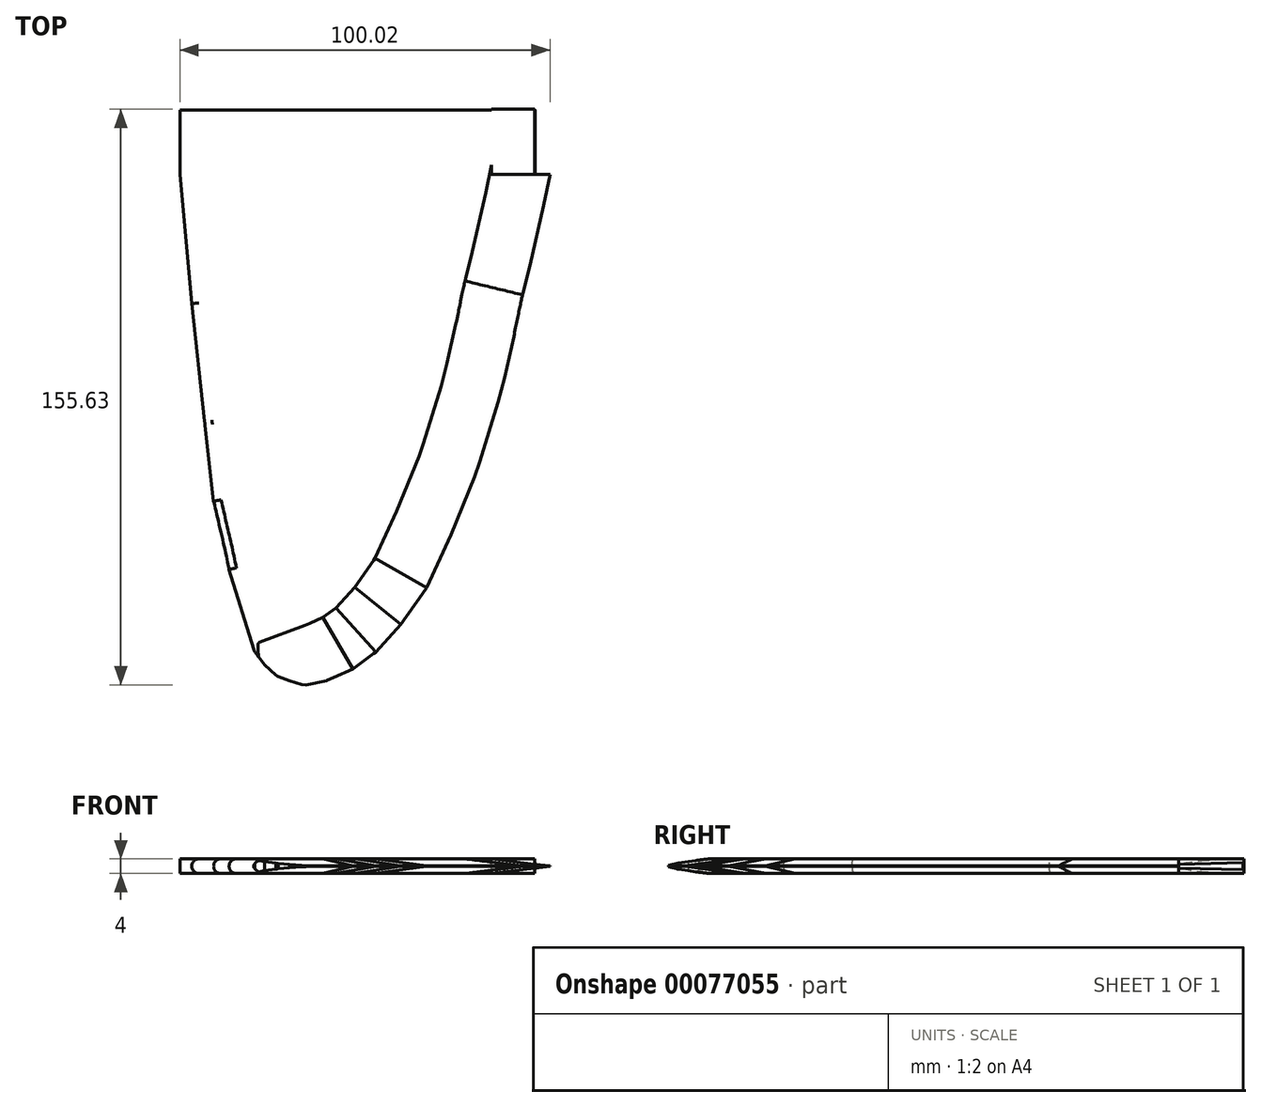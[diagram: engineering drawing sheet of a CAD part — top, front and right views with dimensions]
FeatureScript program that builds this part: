
annotation { "Feature Type Name" : "Feature", "Feature Type Description" : "" }
export const myFeature = defineFeature(function(context is Context, id is Id, definition is map)
    precondition{}
    {
        {
            var Q0;
            Q0=qCreatedBy(makeId("Top.planeOp"),FACE);
            var sketch = newSketch(context, id + "F0", { "sketchPlane" : qUnion([Q0])});
            skLineSegment(sketch, "E0", {"start": v(-143.06, 60.22) * mm, "end": v(-139.92, 25.33) * mm});
            skLineSegment(sketch, "E1", {"start": v(-139.92, 25.33) * mm, "end": v(-136.43, -6.42) * mm});
            skLineSegment(sketch, "E2", {"start": v(-136.43, -6.42) * mm, "end": v(-133.98, -28.05) * mm});
            skLineSegment(sketch, "E3", {"start": v(-133.98, -28.05) * mm, "end": v(-129.8, -46.54) * mm});
            skLineSegment(sketch, "E4", {"start": v(-129.8, -46.54) * mm, "end": v(-123.17, -68.17) * mm});
            skLineSegment(sketch, "E5", {"start": v(-116.54, -75.5) * mm, "end": v(-109.91, -77.94) * mm});
            skLineSegment(sketch, "E6", {"start": v(-109.91, -77.94) * mm, "end": v(-103.28, -76.55) * mm});
            skLineSegment(sketch, "E7", {"start": v(-103.28, -76.55) * mm, "end": v(-96.3, -73.4) * mm});
            skLineSegment(sketch, "E8", {"start": v(-96.3, -73.4) * mm, "end": v(-89.68, -68.52) * mm});
            skLineSegment(sketch, "E9", {"start": v(-89.68, -68.52) * mm, "end": v(-83.05, -61.2) * mm});
            skLineSegment(sketch, "E10", {"start": v(-83.05, -61.2) * mm, "end": v(-76.42, -51.43) * mm});
            skLineSegment(sketch, "E11", {"start": v(-76.42, -51.43) * mm, "end": v(-69.79, -37.12) * mm});
            skLineSegment(sketch, "E12", {"start": v(-69.79, -37.12) * mm, "end": v(-62.81, -20.03) * mm});
            skLineSegment(sketch, "E13", {"start": v(-62.81, -20.03) * mm, "end": v(-56.18, 1.6) * mm});
            skLineSegment(sketch, "E14", {"start": v(-56.18, 1.6) * mm, "end": v(-49.55, 30.91) * mm});
            skLineSegment(sketch, "E15", {"start": v(-49.55, 30.91) * mm, "end": v(-42.92, 60.22) * mm});
            skLineSegment(sketch, "E16", {"start": v(-42.92, 60.22) * mm, "end": v(-47.11, 60.22) * mm});
            skLineSegment(sketch, "E17", {"start": v(-47.11, 60.22) * mm, "end": v(-47.11, 77.66) * mm});
            skLineSegment(sketch, "E18", {"start": v(-47.11, 77.66) * mm, "end": v(-143.06, 77.66) * mm});
            skLineSegment(sketch, "E19", {"start": v(-143.06, 77.66) * mm, "end": v(-143.06, 60.22) * mm});
            skLineSegment(sketch, "E20", {"start": v(-143.08, 77.94) * mm, "end": v(-143.08, 57.6) * mm});
            skLineSegment(sketch, "E21", {"start": v(-143.08, 57.6) * mm, "end": v(-139.68, 22.63) * mm});
            skLineSegment(sketch, "E22", {"start": v(-139.68, 22.63) * mm, "end": v(-136.03, -10.25) * mm});
            skLineSegment(sketch, "E23", {"start": v(-136.03, -10.25) * mm, "end": v(-134.73, -24.08) * mm});
            skLineSegment(sketch, "E24", {"start": v(-134.73, -24.08) * mm, "end": v(-134.07, -28.51) * mm});
            skLineSegment(sketch, "E25", {"start": v(-134.07, -28.51) * mm, "end": v(-129.64, -47.95) * mm});
            skLineSegment(sketch, "E26", {"start": v(-129.64, -47.95) * mm, "end": v(-123.12, -68.44) * mm});
            skLineSegment(sketch, "E27", {"start": v(-123.12, -68.44) * mm, "end": v(-120.25, -72.35) * mm});
            skLineSegment(sketch, "E28", {"start": v(-120.25, -72.35) * mm, "end": v(-116.6, -75.61) * mm});
            skLineSegment(sketch, "E29", {"start": v(-116.6, -75.61) * mm, "end": v(-110.2, -77.7) * mm});
            skLineSegment(sketch, "E30", {"start": v(-110.2, -77.7) * mm, "end": v(-106.8, -77.83) * mm});
            skLineSegment(sketch, "E31", {"start": v(-106.8, -77.83) * mm, "end": v(-103.28, -76.52) * mm});
            skLineSegment(sketch, "E32", {"start": v(-103.28, -76.52) * mm, "end": v(-96.1, -73.4) * mm});
            skLineSegment(sketch, "E33", {"start": v(-96.1, -73.4) * mm, "end": v(-90.1, -68.83) * mm});
            skLineSegment(sketch, "E34", {"start": v(-90.1, -68.83) * mm, "end": v(-83.32, -61.4) * mm});
            skLineSegment(sketch, "E35", {"start": v(-83.32, -61.4) * mm, "end": v(-76.15, -51.08) * mm});
            skLineSegment(sketch, "E36", {"start": v(-76.15, -51.08) * mm, "end": v(-71.32, -40.78) * mm});
            skLineSegment(sketch, "E37", {"start": v(-71.32, -40.78) * mm, "end": v(-66.89, -30.6) * mm});
            skLineSegment(sketch, "E38", {"start": v(-66.89, -30.6) * mm, "end": v(-63.5, -21.73) * mm});
            skLineSegment(sketch, "E39", {"start": v(-63.5, -21.73) * mm, "end": v(-60.62, -13.38) * mm});
            skLineSegment(sketch, "E40", {"start": v(-60.62, -13.38) * mm, "end": v(-57.23, -1.9) * mm});
            skLineSegment(sketch, "E41", {"start": v(-57.23, -1.9) * mm, "end": v(-54.36, 9.06) * mm});
            skLineSegment(sketch, "E42", {"start": v(-54.36, 9.06) * mm, "end": v(-50.45, 27.71) * mm});
            skLineSegment(sketch, "E43", {"start": v(-50.45, 27.71) * mm, "end": v(-46.92, 41.94) * mm});
            skLineSegment(sketch, "E44", {"start": v(-46.92, 41.94) * mm, "end": v(-43.01, 60.33) * mm});
            skLineSegment(sketch, "E45", {"start": v(-43.01, 60.33) * mm, "end": v(-47.06, 60.46) * mm});
            skLineSegment(sketch, "E46", {"start": v(-47.06, 60.46) * mm, "end": v(-47.06, 77.94) * mm});
            skLineSegment(sketch, "E47", {"start": v(-47.06, 77.94) * mm, "end": v(-143.08, 77.94) * mm});
            skFitSpline(sketch, "E48", {"points": [v(-143.06, 60.22) * mm, v(-143.08, 57.6) * mm, v(-139.92, 25.33) * mm, v(-139.68, 22.63) * mm, v(-136.43, -6.42) * mm, v(-136.03, -10.25) * mm, v(-134.73, -24.08) * mm, v(-133.98, -28.05) * mm, v(-129.8, -46.54) * mm, v(-129.64, -47.95) * mm, v(-123.17, -68.17) * mm, v(-120.25, -72.35) * mm, v(-116.54, -75.5) * mm, v(-109.91, -77.94) * mm, v(-106.8, -77.83) * mm, v(-103.28, -76.55) * mm, v(-96.1, -73.4) * mm, v(-90.1, -68.83) * mm, v(-83.32, -61.4) * mm, v(-76.15, -51.08) * mm, v(-71.32, -40.78) * mm, v(-69.79, -37.12) * mm, v(-66.89, -30.6) * mm, v(-63.5, -21.73) * mm, v(-62.81, -20.03) * mm, v(-60.62, -13.38) * mm, v(-57.23, -1.9) * mm, v(-56.18, 1.6) * mm, v(-54.36, 9.06) * mm, v(-50.45, 27.71) * mm, v(-49.55, 30.91) * mm, v(-46.92, 41.94) * mm, v(-42.92, 60.22) * mm], "startDerivative": vector(-10.44, -78.3) * mm, "endDerivative": vector(86.1, 398.54) * mm});
            skSolve(sketch);
        }
        {
            var Q0;
            Q0=makeQuery(id+"F0.imprint","IMPRINT",FACE,{"disambiguationData":[TD([[makeQuery(id+"F0.imprint","IMPRINT",EDGE,{"derivedFrom":sQuery(id+"F0.wireOp",EDGE,"E0")}),1.0]])]});
            extrude(context, id + "F1", {"entities" : qUnion([Q0]), "depth" : 2 * mm});
        }
        {
            var Q0;
            Q0=makeQuery(id+"F1.opExtrude","CAP_EDGE",EDGE,{"disambiguationData":[OSD([sQuery(id+"F0.wireOp",EDGE,"E44")])],"isStart":false});
            var Q1;
            Q1=makeQuery(id+"F1.opExtrude","CAP_EDGE",EDGE,{"disambiguationData":[OSD([sQuery(id+"F0.wireOp",EDGE,"E15")])],"isStart":false});
            var Q2;
            Q2=makeQuery(id+"F1.opExtrude","CAP_EDGE",EDGE,{"disambiguationData":[OSD([sQuery(id+"F0.wireOp",EDGE,"E43")])],"isStart":false});
            var Q3;
            {var subQ0=sQuery(id+"F0.wireOp",EDGE,"E48");var subQ1=sQuery(id+"F0.wireOp",EDGE,"E43");Q3=makeQuery(id+"F1.opExtrude","CAP_EDGE",EDGE,{"disambiguationData":[OSD([subQ0]),TDD([makeQuery(id+"F0.imprint","IMPRINT",EDGE,{"disambiguationData":[TD([[makeQuery(id+"F0.imprint","INTERSECT",VERTEX,{"derivedFrom":[sQuery(id+"F0.wireOp",EDGE,"E14"),subQ0]}),-1.0]])],"derivedFrom":subQ0}),makeQuery(id+"F0.imprint","IMPRINT",EDGE,{"disambiguationData":[TD([[makeQuery(id+"F0.imprint","INTERSECT",VERTEX,{"derivedFrom":[subQ1,subQ0]}),1.0]])],"derivedFrom":subQ0})])],"isStart":false});}
            var Q4;
            Q4=makeQuery(id+"F1.opExtrude","CAP_EDGE",EDGE,{"disambiguationData":[OSD([sQuery(id+"F0.wireOp",EDGE,"E14")])],"isStart":false});
            var Q5;
            Q5=makeQuery(id+"F1.opExtrude","CAP_EDGE",EDGE,{"disambiguationData":[OSD([sQuery(id+"F0.wireOp",EDGE,"E41")])],"isStart":false});
            var Q6;
            Q6=makeQuery(id+"F1.opExtrude","CAP_EDGE",EDGE,{"disambiguationData":[OSD([sQuery(id+"F0.wireOp",EDGE,"E13")])],"isStart":false});
            var Q7;
            Q7=makeQuery(id+"F1.opExtrude","CAP_EDGE",EDGE,{"disambiguationData":[OSD([sQuery(id+"F0.wireOp",EDGE,"E39")])],"isStart":false});
            var Q8;
            Q8=makeQuery(id+"F1.opExtrude","CAP_EDGE",EDGE,{"disambiguationData":[OSD([sQuery(id+"F0.wireOp",EDGE,"E12")])],"isStart":false});
            var Q9;
            Q9=makeQuery(id+"F1.opExtrude","CAP_EDGE",EDGE,{"disambiguationData":[OSD([sQuery(id+"F0.wireOp",EDGE,"E11")])],"isStart":false});
            var Q10;
            Q10=makeQuery(id+"F1.opExtrude","CAP_EDGE",EDGE,{"disambiguationData":[OSD([sQuery(id+"F0.wireOp",EDGE,"E10")])],"isStart":false});
            var Q11;
            Q11=makeQuery(id+"F1.opExtrude","CAP_EDGE",EDGE,{"disambiguationData":[OSD([sQuery(id+"F0.wireOp",EDGE,"E35")])],"isStart":false});
            var Q12;
            Q12=makeQuery(id+"F1.opExtrude","CAP_EDGE",EDGE,{"disambiguationData":[OSD([sQuery(id+"F0.wireOp",EDGE,"E34")])],"isStart":false});
            var Q13;
            Q13=makeQuery(id+"F1.opExtrude","CAP_EDGE",EDGE,{"disambiguationData":[OSD([sQuery(id+"F0.wireOp",EDGE,"E33")])],"isStart":false});
            var Q14;
            Q14=makeQuery(id+"F1.opExtrude","CAP_EDGE",EDGE,{"disambiguationData":[OSD([sQuery(id+"F0.wireOp",EDGE,"E8")])],"isStart":false});
            var Q15;
            Q15=makeQuery(id+"F1.opExtrude","CAP_EDGE",EDGE,{"disambiguationData":[OSD([sQuery(id+"F0.wireOp",EDGE,"E7")])],"isStart":false});
            var Q16;
            Q16=makeQuery(id+"F1.opExtrude","CAP_EDGE",EDGE,{"disambiguationData":[OSD([sQuery(id+"F0.wireOp",EDGE,"E32")])],"isStart":false});
            var Q17;
            Q17=makeQuery(id+"F1.opExtrude","CAP_EDGE",EDGE,{"disambiguationData":[OSD([sQuery(id+"F0.wireOp",EDGE,"E31")])],"isStart":false});
            var Q18;
            Q18=makeQuery(id+"F1.opExtrude","CAP_EDGE",EDGE,{"disambiguationData":[OSD([sQuery(id+"F0.wireOp",EDGE,"E6")])],"isStart":false});
            chamfer(context, id + "F2", {"entities" : qUnion([Q0, Q1, Q2, Q3, Q4, Q5, Q6, Q7, Q8, Q9, Q10, Q11, Q12, Q13, Q14, Q15, Q16, Q17, Q18]), "chamferType" : ChamferType.OFFSET_ANGLE, "width" : 16 * mm, "oppositeDirection" : false, "angle" : 7 * degree, "tangentPropagation" : true});
        }
        {
            var Q0;
            Q0=qCreatedBy(makeId("Top.planeOp"),FACE);
            var sketch = newSketch(context, id + "F3", { "sketchPlane" : qUnion([Q0])});
            skLineSegment(sketch, "E49.bottom", {"start": v(-58.84, 77.88) * mm, "end": v(-47.13, 77.88) * mm});
            skLineSegment(sketch, "E49.top", {"start": v(-58.84, 60.24) * mm, "end": v(-47.13, 60.24) * mm});
            skLineSegment(sketch, "E49.left", {"start": v(-58.84, 77.88) * mm, "end": v(-58.84, 60.24) * mm});
            skLineSegment(sketch, "E49.right", {"start": v(-47.13, 77.88) * mm, "end": v(-47.13, 60.24) * mm});
            skSolve(sketch);
        }
        {
            var Q0;
            Q0 = qSketchRegion(id + "F3", true);
            extrude(context, id + "F4", {"entities" : qUnion([Q0]), "operationType" : NewBodyOperationType.ADD, "depth" : 2 * mm});
        }
        {
            var Q0;
            Q0=makeQuery(id+"F1.opExtrude","CAP_EDGE",EDGE,{"disambiguationData":[OSD([sQuery(id+"F0.wireOp",EDGE,"E4")])],"isStart":false});
            var Q1;
            {var subQ0=sQuery(id+"F0.wireOp",EDGE,"E48");var subQ1=sQuery(id+"F0.wireOp",EDGE,"E3");Q1=makeQuery(id+"F1.opExtrude","CAP_EDGE",EDGE,{"disambiguationData":[OSD([subQ0]),TDD([makeQuery(id+"F0.imprint","IMPRINT",EDGE,{"disambiguationData":[TD([[makeQuery(id+"F0.imprint","INTERSECT",VERTEX,{"derivedFrom":[sQuery(id+"F0.wireOp",EDGE,"E2"),subQ1,subQ0]}),-1.0]])],"derivedFrom":subQ0})])],"isStart":false});}
            var Q2;
            Q2=makeQuery(id+"F1.opExtrude","CAP_EDGE",EDGE,{"disambiguationData":[OSD([sQuery(id+"F0.wireOp",EDGE,"E2")])],"isStart":false});
            var Q3;
            Q3=makeQuery(id+"F1.opExtrude","CAP_EDGE",EDGE,{"disambiguationData":[OSD([sQuery(id+"F0.wireOp",EDGE,"E1")])],"isStart":false});
            var Q4;
            Q4=makeQuery(id+"F1.opExtrude","CAP_EDGE",EDGE,{"disambiguationData":[OSD([sQuery(id+"F0.wireOp",EDGE,"E0")])],"isStart":false});
            fillet(context, id + "F5", {"entities" : qUnion([Q0, Q1, Q2, Q3, Q4]), "radius" : 2 * mm, "tangentPropagation" : true, "allowEdgeOverflow" : false});
        }
        {
            var Q0;
            Q0=makeQuery(id+"F1.opExtrude","SWEPT_BODY",BODY,{"disambiguationData":[OSD([sQuery(id+"F0.wireOp",EDGE,"E0"),sQuery(id+"F0.wireOp",EDGE,"E1"),sQuery(id+"F0.wireOp",EDGE,"E2"),sQuery(id+"F0.wireOp",EDGE,"E4"),sQuery(id+"F0.wireOp",EDGE,"E5"),sQuery(id+"F0.wireOp",EDGE,"E6"),sQuery(id+"F0.wireOp",EDGE,"E7"),sQuery(id+"F0.wireOp",EDGE,"E8"),sQuery(id+"F0.wireOp",EDGE,"E10"),sQuery(id+"F0.wireOp",EDGE,"E11"),sQuery(id+"F0.wireOp",EDGE,"E12"),sQuery(id+"F0.wireOp",EDGE,"E13"),sQuery(id+"F0.wireOp",EDGE,"E14"),sQuery(id+"F0.wireOp",EDGE,"E15"),sQuery(id+"F0.wireOp",EDGE,"E16"),sQuery(id+"F0.wireOp",EDGE,"E17"),sQuery(id+"F0.wireOp",EDGE,"E18"),sQuery(id+"F0.wireOp",EDGE,"E19"),sQuery(id+"F0.wireOp",EDGE,"E27"),sQuery(id+"F0.wireOp",EDGE,"E28"),sQuery(id+"F0.wireOp",EDGE,"E29"),sQuery(id+"F0.wireOp",EDGE,"E30"),sQuery(id+"F0.wireOp",EDGE,"E31"),sQuery(id+"F0.wireOp",EDGE,"E32"),sQuery(id+"F0.wireOp",EDGE,"E33"),sQuery(id+"F0.wireOp",EDGE,"E34"),sQuery(id+"F0.wireOp",EDGE,"E35"),sQuery(id+"F0.wireOp",EDGE,"E39"),sQuery(id+"F0.wireOp",EDGE,"E41"),sQuery(id+"F0.wireOp",EDGE,"E43"),sQuery(id+"F0.wireOp",EDGE,"E44"),sQuery(id+"F0.wireOp",EDGE,"E48")])]});
            var Q1;
            Q1=qCreatedBy(makeId("Top.planeOp"),FACE);
            mirror(context, id + "F6", {"operationType" : NewBodyOperationType.ADD, "entities" : qUnion([Q0]), "mirrorPlane" : qUnion([Q1])});
        }
    });
